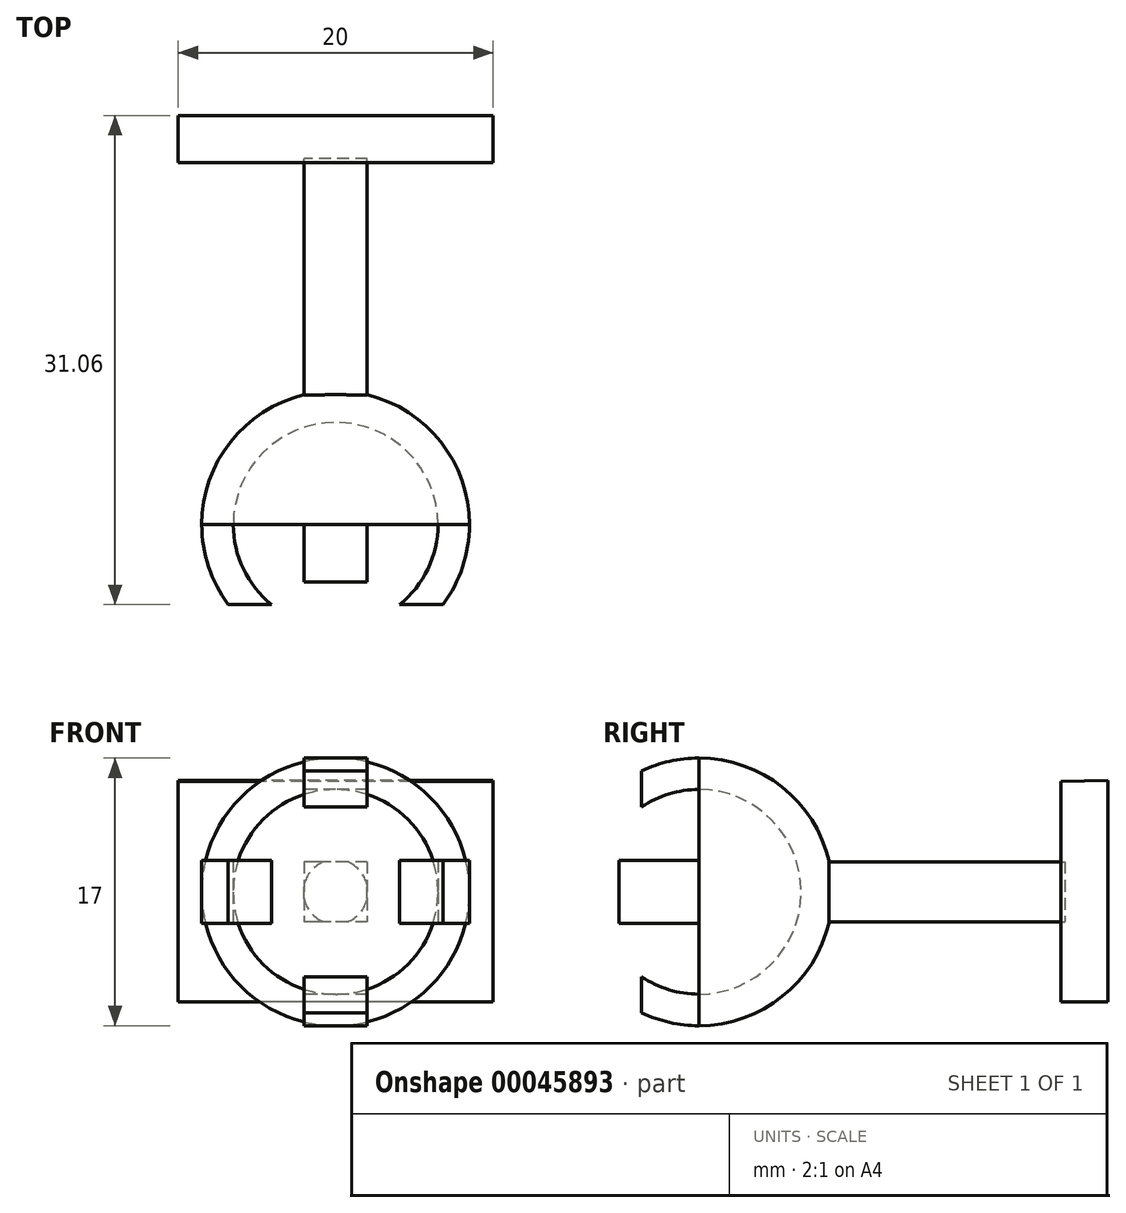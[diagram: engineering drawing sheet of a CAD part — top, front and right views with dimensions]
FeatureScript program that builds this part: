
annotation { "Feature Type Name" : "Feature", "Feature Type Description" : "" }
export const myFeature = defineFeature(function(context is Context, id is Id, definition is map)
    precondition{}
    {
        {
            var Q0;
            Q0=qCreatedBy(makeId("Top.planeOp"),FACE);
            var sketch = newSketch(context, id + "F0", { "sketchPlane" : qUnion([Q0])});
            skArc(sketch, "E0", {"start": v(6.5, 0) * mm, "mid": v(0, 6.5) * mm, "end": v(-6.5, 0) * mm});
            skArc(sketch, "E1", {"start": v(8.5, 0) * mm, "mid": v(0, 8.5) * mm, "end": v(-8.5, 0) * mm});
            skLineSegment(sketch, "E2", {"start": v(-8.5, 0) * mm, "end": v(-6.5, 0) * mm});
            skLineSegment(sketch, "E3.trimOffspring", {"start": v(6.5, 0) * mm, "end": v(8.5, 0) * mm});
            skSolve(sketch);
        }
        {
            var Q0;
            Q0=makeQuery(id+"F0.imprint","IMPRINT",FACE,{"disambiguationData":[TD([[makeQuery(id+"F0.imprint","IMPRINT",EDGE,{"derivedFrom":sQuery(id+"F0.wireOp",EDGE,"E0")}),-1.0]])]});
            var Q1;
            Q1=sQuery(id+"F0.wireOp",EDGE,"E3.trimOffspring");
            revolve(context, id + "F1", {"entities" : qUnion([Q0]), "axis" : qUnion([Q1]), "revolveType" : RevolveType.SYMMETRIC, "angle" : 180 * degree});
        }
        {
            var Q0;
            Q0=qCreatedBy(makeId("Top.planeOp"),FACE);
            var sketch = newSketch(context, id + "F2", { "sketchPlane" : qUnion([Q0])});
            skArc(sketch, "E4", {"start": v(-8.5, 0) * mm, "mid": v(-8.07, -2.67) * mm, "end": v(-6.82, -5.07) * mm});
            skArc(sketch, "E5", {"start": v(-6.5, 0) * mm, "mid": v(-5.86, -2.81) * mm, "end": v(-4.07, -5.07) * mm});
            skLineSegment(sketch, "E6", {"start": v(-8.5, 0) * mm, "end": v(8.5, 0) * mm});
            skArc(sketch, "E7.trimOffspring", {"start": v(6.82, -5.07) * mm, "mid": v(8.07, -2.67) * mm, "end": v(8.5, 0) * mm});
            skArc(sketch, "E8.trimOffspring", {"start": v(4.07, -5.07) * mm, "mid": v(5.86, -2.81) * mm, "end": v(6.5, 0) * mm});
            skPoint(sketch, "E9.orphan", {"position": v(4.07, 0) * mm});
            skPoint(sketch, "E10.orphan", {"position": v(-4.07, 0) * mm});
            skLineSegment(sketch, "E11", {"start": v(-4.07, -5.07) * mm, "end": v(-6.82, -5.07) * mm});
            skLineSegment(sketch, "E12", {"start": v(4.07, -5.07) * mm, "end": v(6.82, -5.07) * mm});
            skPoint(sketch, "E13.MirrorCS.end.orphan", {"position": v(4.07, -7.46) * mm});
            skPoint(sketch, "E14.orphan", {"position": v(-4.07, -7.46) * mm});
            skSolve(sketch);
        }
        {
            var Q0;
            Q0 = qSketchRegion(id + "F2", true);
            extrude(context, id + "F3", {"entities" : qUnion([Q0]), "operationType" : NewBodyOperationType.ADD, "endBound" : BoundingType.SYMMETRIC, "depth" : 4 * mm});
        }
        {
            var Q0;
            Q0=qCreatedBy(makeId("Right.planeOp"),FACE);
            var sketch = newSketch(context, id + "F4", { "sketchPlane" : qUnion([Q0])});
            skArc(sketch, "E15", {"start": v(0, 8.5) * mm, "mid": v(-1.86, 8.3) * mm, "end": v(-3.63, 7.69) * mm});
            skArc(sketch, "E16", {"start": v(0, 6.5) * mm, "mid": v(-1.9, 6.22) * mm, "end": v(-3.63, 5.4) * mm});
            skLineSegment(sketch, "E17", {"start": v(0, -8.5) * mm, "end": v(0, 8.5) * mm});
            skLineSegment(sketch, "E18", {"start": v(-3.63, 5.4) * mm, "end": v(-3.63, 7.69) * mm});
            skLineSegment(sketch, "E19", {"start": v(-3.63, -5.4) * mm, "end": v(-3.63, -7.69) * mm});
            skPoint(sketch, "E20.end.orphan", {"position": v(0, -5.4) * mm});
            skPoint(sketch, "E21.MirrorCS.end.orphan", {"position": v(0, 5.4) * mm});
            skArc(sketch, "E22.trimOffspring", {"start": v(-3.63, -7.69) * mm, "mid": v(-1.86, -8.3) * mm, "end": v(0, -8.5) * mm});
            skArc(sketch, "E23.trimOffspring", {"start": v(-3.63, -5.4) * mm, "mid": v(-1.9, -6.22) * mm, "end": v(0, -6.5) * mm});
            skSolve(sketch);
        }
        {
            var Q0;
            Q0 = qSketchRegion(id + "F4", true);
            extrude(context, id + "F5", {"entities" : qUnion([Q0]), "operationType" : NewBodyOperationType.ADD, "endBound" : BoundingType.SYMMETRIC, "depth" : 4 * mm});
        }
        {
            var Q0;
            Q0=qCreatedBy(makeId("Right.planeOp"),FACE);
            var sketch = newSketch(context, id + "F6", { "sketchPlane" : qUnion([Q0])});
            skLineSegment(sketch, "E24", {"start": v(8.25, 1.91) * mm, "end": v(23.25, 1.91) * mm});
            skLineSegment(sketch, "E25.MirrorCS", {"start": v(8.25, -1.91) * mm, "end": v(23.25, -1.91) * mm});
            skLineSegment(sketch, "E26", {"start": v(23.25, 1.91) * mm, "end": v(23.25, -1.91) * mm});
            skLineSegment(sketch, "E27", {"start": v(8.25, 1.91) * mm, "end": v(8.25, -1.91) * mm});
            skSolve(sketch);
        }
        {
            var Q0;
            Q0 = qSketchRegion(id + "F6", true);
            extrude(context, id + "F7", {"entities" : qUnion([Q0]), "operationType" : NewBodyOperationType.ADD, "endBound" : BoundingType.SYMMETRIC, "depth" : 4 * mm});
        }
        {
            var Q0;
            Q0=qCreatedBy(makeId("Right.planeOp"),FACE);
            var sketch = newSketch(context, id + "F8", { "sketchPlane" : qUnion([Q0])});
            skLineSegment(sketch, "E28", {"start": v(23, 0) * mm, "end": v(23, -7) * mm});
            skLineSegment(sketch, "E29", {"start": v(23, 0) * mm, "end": v(23, 7) * mm});
            skLineSegment(sketch, "E30", {"start": v(23, -7) * mm, "end": v(26, -7) * mm});
            skLineSegment(sketch, "E31", {"start": v(26, -7) * mm, "end": v(26, 7.07) * mm});
            skLineSegment(sketch, "E32", {"start": v(26, 7.07) * mm, "end": v(23, 7) * mm});
            skSolve(sketch);
        }
        {
            var Q0;
            Q0 = qSketchRegion(id + "F8", true);
            extrude(context, id + "F9", {"entities" : qUnion([Q0]), "endBound" : BoundingType.SYMMETRIC, "depth" : 20 * mm});
        }
        {
            var Q0;
            Q0=sQuery(id+"F8.wireOp",EDGE,"E31");
            extrude(context, id + "F10", {"bodyType" : ToolBodyType.SURFACE, "surfaceEntities" : qUnion([Q0]), "endBound" : BoundingType.SYMMETRIC, "depth" : 4 * mm});
        }
    });
